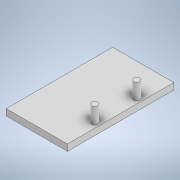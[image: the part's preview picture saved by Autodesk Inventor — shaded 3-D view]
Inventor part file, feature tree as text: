
AUTODESK INVENTOR PART (.ipt)
format: ipt  version: 2021 (Build 250183000, 183)  size: 115,712 bytes
history: native  units: mm
features: extrude x3, sketch x3, other x1
ambient origin geometry x8: Origin, YZ Plane, XZ Plane, XY Plane, X Axis, Y Axis, Z Axis, Center Point
bodies: Body1 (feature_tree)
feature tree (7):
  other  "Sólido1"
  extrude  "Extrusión1"  Depth=33.0mm
  extrude  "Extrusión2"  Depth=10.0mm
  extrude  "Extrusión3"  Depth=5.0mm
  sketch  "Boceto1"  dims[d0=3.0mm d1=33.0mm]
  sketch  "Boceto2"  dims[d2=2.0mm d3=0.0mm d4=10.0mm]
  sketch  "Boceto3"  dims[d5=10.0mm d8=1.9mm d9=1.9mm d10=5.0mm d11=0.0mm d12=16.0mm d13=0.0mm]
